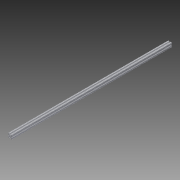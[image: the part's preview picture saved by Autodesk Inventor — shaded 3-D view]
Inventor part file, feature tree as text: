
AUTODESK INVENTOR PART (.ipt)
format: ipt  version: 2013 (Build 170138000, 138)  size: 286,208 bytes
history: native  units: in
note: dims shown in document units (in); Inventor stores cm internally (conversion verified against a paired STEP export)
features: extrude x1, sketch x1
ambient origin geometry x8: Origin, YZ Plane, XZ Plane, XY Plane, X Axis, Y Axis, Z Axis, Center Point
bodies: Solid1 (feature_tree)
feature tree (2):
  extrude  "Extrusion1"  [1 undecoded]
  sketch  "Sketch1"  dims[d0=60.0in d1=0.0in]
note: 1 required parameter value undecoded (feature->parameter linkage not recoverable at this tier; creation-order binding heuristic only, values carry confidence <= 0.55)
